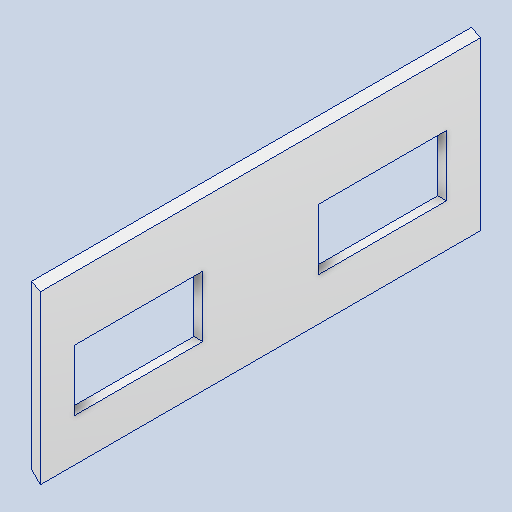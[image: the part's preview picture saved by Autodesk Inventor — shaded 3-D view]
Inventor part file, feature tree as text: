
AUTODESK INVENTOR PART (.ipt)
format: ipt  version: 2023 (Build 270158000, 158)  size: 136,192 bytes
history: native  units: mm
features: other x3, extrude x3, sketch x3, chamfer x1, reference x1
ambient origin geometry x8: Origin, YZ Plane, XZ Plane, XY Plane, X Axis, Y Axis, Z Axis, Center Point
bodies: Body1 (feature_tree)
feature tree (11):
  other  "Bryła1"
  extrude  "Wyciągnięcie proste1"  Depth=2.0mm TaperAngle=0.0deg
  chamfer  "Faza1"  Distance=2.0mm Angle=45.0deg
  extrude  "Wyciągnięcie proste2"  TaperAngle=0.0deg  [1 undecoded]
  extrude  "Wyciągnięcie proste3"  Depth=2.0mm
  sketch  "Szkic1"
  sketch  "Szkic2"
  reference  "Odniesienie1"
  sketch  "Szkic3"
  other  "Zespół1"
  other  "sciana_prawa_nowa:1"
note: 1 required parameter value undecoded (feature->parameter linkage not recoverable at this tier; creation-order binding heuristic only, values carry confidence <= 0.55)
